# Revit family: Hushmeet.open EN3
name_source: partatom
category: Casework
revit_build: Autodesk Revit 2018 (Build: 20190510_1515(x64)
units: mm (PartAtom-declared; Revit-internal decimal feet)

## family parameters
Always vertical = Yes
Cut with Voids When Loaded = No
OmniClass Number = 23.40.35.00
OmniClass Title = Casework
Room Calculation Point = Yes
Shared = No
Work Plane-Based = No

## types (1)
- HUSH MEET OPEN
    Assembly Code = E2010200
    Back glass colour = Glass Clear PRZ
    Case = Cosmos Grey AGC
    Catalogue = https://hushoffice.com
    Configurator = https://mikomax.actumwork.pl
    Construction Type = Defined construction
    Depth = 1390 mm  [stored 4.56037 ft]
    Description = Independent spaces for solo working and meetings, including virtual ones
    E AU = Power module : AU Type (1 x electric,1 x USB A,1 x USB C,1 x RJ45) - black
    E CH = Power module : CH (1 x electric, 2 x USB, 2 x RJ45)
    E DE = Power module : DE (1 x electric, 2 x USB, 2 x RJ45)
    E DK = Power module : DK (1 x electric, 2 x USB, 2 x RJ45)
    E GB = Power module : GB (1 x electric, 2 x USB, 2 x RJ45)
    E GB2 = Power module : GB Type (1 x electric,1 x USB A,1 x USB C,1 x RJ45) - black
    E PL/FR = Power module : PL/FR (1 x electric, 2 x USB, 2 x RJ45)
    E PL/FR2 = Power module : PL/FR Type (1 x electric,1 x USB A,1 x USB C,1 x RJ45) - black
    E US = Power module : US Type (1 x electric,1 x USB A,1 x USB C,1 x RJ45) - black
    Fabric = PETRUS Amberglow TAG
    Fabric (detail) = PETRUS Amberglow TAG
    Finish = Defined materials
    Height = 2300 mm  [stored 7.54593 ft]
    IfcExportAs = IfcFurniture
    Manufacturer = Mikomax Smart Office
    Middle column = Cosmos Grey AGC
    Model = HUSH MEET OPEN
    Type Image = hush-meet-open.jpeg
    URL = https://hushoffice.com
    Width = 2150 mm  [stored 7.05381 ft]

note: [stored X ft] marks values corroborated as IEEE doubles in the binary element streams (Revit-internal decimal feet)

## geometry (parser evidence)
native form markers: Sweep x32
no freeform markers — native parametric forms only
